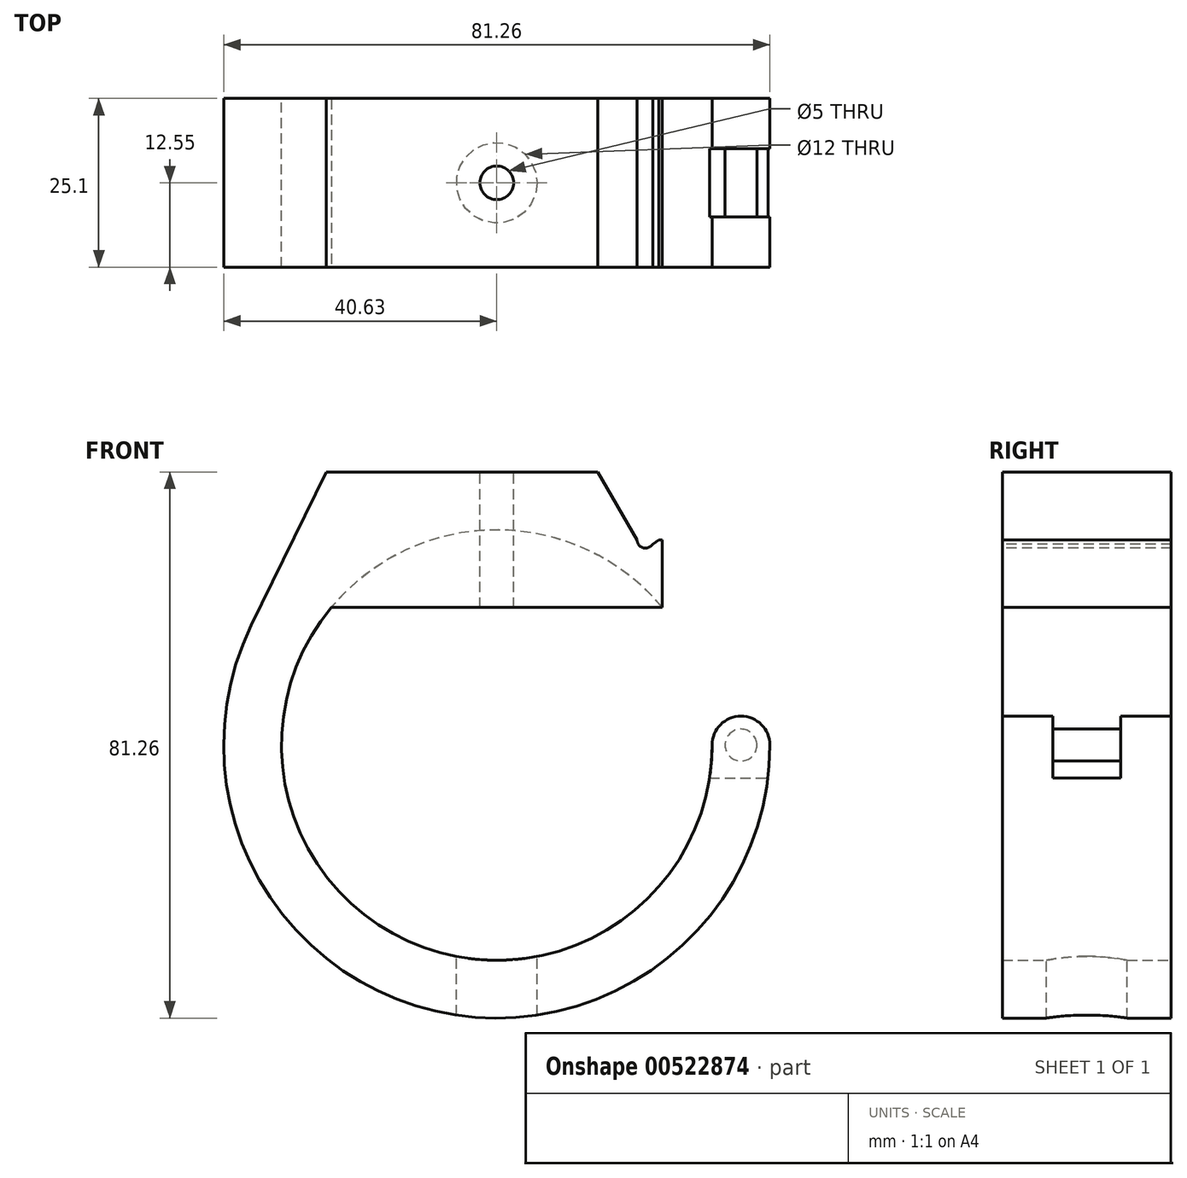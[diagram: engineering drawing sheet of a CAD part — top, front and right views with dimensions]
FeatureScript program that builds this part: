
annotation { "Feature Type Name" : "Feature", "Feature Type Description" : "" }
export const myFeature = defineFeature(function(context is Context, id is Id, definition is map)
    precondition{}
    {
        {
            var Q0;
            Q0=qCreatedBy(makeId("Front.planeOp"),FACE);
            var sketch = newSketch(context, id + "F0", { "sketchPlane" : qUnion([Q0])});
            skLineSegment(sketch, "E0.bottom", {"start": v(-25.4, 40.62) * mm, "end": v(24.6, 40.62) * mm});
            skLineSegment(sketch, "E0.left", {"start": v(-25.4, 40.62) * mm, "end": v(-25.4, 31.71) * mm});
            skLineSegment(sketch, "E0.right", {"start": v(24.6, 40.62) * mm, "end": v(24.6, 32.32) * mm});
            skPoint(sketch, "E0.middle", {"position": v(0, 0) * mm});
            skArc(sketch, "E1", {"start": v(-25.4, 31.71) * mm, "mid": v(0.5, -40.62) * mm, "end": v(24.6, 32.32) * mm});
            skCircle(sketch, "E2", {"center": v(0, 0) * mm, "radius": 32.02 * mm});
            skLineSegment(sketch, "E3", {"start": v(32.02, 0) * mm, "end": v(40.62, 0) * mm});
            skCircle(sketch, "E4", {"center": v(36.32, 0) * mm, "radius": 2.38 * mm});
            skCircle(sketch, "E5", {"center": v(36.32, 0) * mm, "radius": 4.3 * mm});
            skLineSegment(sketch, "E6", {"start": v(24.6, 32.32) * mm, "end": v(24.6, 20.49) * mm});
            skLineSegment(sketch, "E7", {"start": v(40.33, -4.92) * mm, "end": v(31.64, -4.92) * mm});
            skLineSegment(sketch, "E8", {"start": v(-25.4, 40.62) * mm, "end": v(-36.52, 17.8) * mm});
            skSolve(sketch);
        }
        {
            var Q0;
            Q0=makeQuery(id+"F0.imprint","IMPRINT",FACE,{"disambiguationData":[TD([[makeQuery(id+"F0.imprint","IMPRINT",EDGE,{"derivedFrom":sQuery(id+"F0.wireOp",EDGE,"E0.bottom")}),-1.0]])]});
            var Q1;
            {var subQ4=sQuery(id+"F0.wireOp",EDGE,"E7");Q1=makeQuery(id+"F0.imprint","IMPRINT",FACE,{"disambiguationData":[TD([[makeQuery(id+"F0.imprint","IMPRINT",EDGE,{"derivedFrom":subQ4}),-1.0]])]});}
            var Q2;
            {var subQ1=sQuery(id+"F0.wireOp",EDGE,"E3");var subQ3=sQuery(id+"F0.wireOp",EDGE,"E4");var subQ4=makeQuery(id+"F0.imprint","INTERSECT",VERTEX,{"disambiguationData":[OD(0.0)],"derivedFrom":[subQ1,subQ3]});Q2=makeQuery(id+"F0.imprint","IMPRINT",FACE,{"disambiguationData":[TD([[makeQuery(id+"F0.imprint","IMPRINT",EDGE,{"disambiguationData":[TD([[subQ4,1.0]])],"derivedFrom":subQ3}),-1.0]])]});}
            var Q3;
            {var subQ1=sQuery(id+"F0.wireOp",EDGE,"E3");var subQ3=sQuery(id+"F0.wireOp",EDGE,"E4");var subQ4=makeQuery(id+"F0.imprint","INTERSECT",VERTEX,{"disambiguationData":[OD(0.0)],"derivedFrom":[subQ1,subQ3]});Q3=makeQuery(id+"F0.imprint","IMPRINT",FACE,{"disambiguationData":[TD([[makeQuery(id+"F0.imprint","IMPRINT",EDGE,{"disambiguationData":[TD([[subQ4,-1.0]])],"derivedFrom":subQ3}),-1.0]])]});}
            extrude(context, id + "F1", {"entities" : qUnion([Q0, Q1, Q2, Q3]), "depth" : 7.5 * mm, "offsetDistance" : 25 * mm});
        }
        {
            var Q0;
            Q0=makeQuery(id+"F0.imprint","IMPRINT",FACE,{"disambiguationData":[TD([[makeQuery(id+"F0.imprint","IMPRINT",EDGE,{"derivedFrom":sQuery(id+"F0.wireOp",EDGE,"E0.bottom")}),-1.0]])]});
            extrude(context, id + "F2", {"entities" : qUnion([Q0]), "operationType" : NewBodyOperationType.ADD, "depth" : 17.6 * mm, "offsetDistance" : 25 * mm});
        }
        {
            var Q0;
            Q0=makeQuery(id+"F2.opExtrude","CAP_FACE",FACE,{"disambiguationData":[OSD([sQuery(id+"F0.wireOp",EDGE,"E0.bottom"),sQuery(id+"F0.wireOp",EDGE,"E0.left"),sQuery(id+"F0.wireOp",EDGE,"E0.right"),sQuery(id+"F0.wireOp",EDGE,"E1"),sQuery(id+"F0.wireOp",EDGE,"E2"),sQuery(id+"F0.wireOp",EDGE,"E6"),sQuery(id+"F0.wireOp",EDGE,"E7")])],"isStart":false});
            var sketch = newSketch(context, id + "F3", { "sketchPlane" : qUnion([Q0])});
            skLineSegment(sketch, "E9.bottom", {"start": v(-25.4, 40.63) * mm, "end": v(24.6, 40.63) * mm});
            skLineSegment(sketch, "E9.left", {"start": v(-25.4, 40.63) * mm, "end": v(-25.4, 31.71) * mm});
            skLineSegment(sketch, "E9.right", {"start": v(24.6, 40.63) * mm, "end": v(24.6, 32.32) * mm});
            skPoint(sketch, "E9.middle", {"position": v(0, 0) * mm});
            skArc(sketch, "E10", {"start": v(-25.4, 31.71) * mm, "mid": v(0.5, -40.62) * mm, "end": v(24.6, 32.32) * mm});
            skCircle(sketch, "E11", {"center": v(0, 0) * mm, "radius": 32.02 * mm});
            skLineSegment(sketch, "E12", {"start": v(32.02, 0) * mm, "end": v(40.63, 0) * mm});
            skCircle(sketch, "E13", {"center": v(36.32, 0) * mm, "radius": 2.38 * mm});
            skCircle(sketch, "E14", {"center": v(36.32, 0) * mm, "radius": 4.3 * mm});
            skLineSegment(sketch, "E15", {"start": v(24.6, 32.32) * mm, "end": v(24.6, 20.49) * mm});
            skLineSegment(sketch, "E16", {"start": v(40.33, -4.92) * mm, "end": v(31.64, -4.92) * mm});
            skSolve(sketch);
        }
        {
            var Q0;
            Q0=makeQuery(id+"F3.imprint","IMPRINT",FACE,{"disambiguationData":[TD([[makeQuery(id+"F3.imprint","IMPRINT",EDGE,{"derivedFrom":sQuery(id+"F3.wireOp",EDGE,"E9.bottom")}),-1.0]])]});
            var Q1;
            {var subQ0=sQuery(id+"F3.wireOp",EDGE,"E16");Q1=makeQuery(id+"F3.imprint","IMPRINT",FACE,{"disambiguationData":[TD([[makeQuery(id+"F3.imprint","IMPRINT",EDGE,{"derivedFrom":subQ0}),-1.0]])]});}
            var Q2;
            {var subQ1=sQuery(id+"F3.wireOp",EDGE,"E12");var subQ3=sQuery(id+"F3.wireOp",EDGE,"E13");var subQ4=makeQuery(id+"F3.imprint","INTERSECT",VERTEX,{"disambiguationData":[OD(0.0)],"derivedFrom":[subQ1,subQ3]});Q2=makeQuery(id+"F3.imprint","IMPRINT",FACE,{"disambiguationData":[TD([[makeQuery(id+"F3.imprint","IMPRINT",EDGE,{"disambiguationData":[TD([[subQ4,-1.0]])],"derivedFrom":subQ3}),-1.0]])]});}
            var Q3;
            {var subQ1=sQuery(id+"F3.wireOp",EDGE,"E12");var subQ3=sQuery(id+"F3.wireOp",EDGE,"E13");var subQ4=makeQuery(id+"F3.imprint","INTERSECT",VERTEX,{"disambiguationData":[OD(0.0)],"derivedFrom":[subQ1,subQ3]});Q3=makeQuery(id+"F3.imprint","IMPRINT",FACE,{"disambiguationData":[TD([[makeQuery(id+"F3.imprint","IMPRINT",EDGE,{"disambiguationData":[TD([[subQ4,1.0]])],"derivedFrom":subQ3}),-1.0]])]});}
            extrude(context, id + "F4", {"entities" : qUnion([Q0, Q1, Q2, Q3]), "operationType" : NewBodyOperationType.ADD, "depth" : 7.5 * mm, "offsetDistance" : 25 * mm});
        }
        {
            var Q0;
            Q0=makeQuery(id+"F4.opExtrude","CAP_FACE",FACE,{"disambiguationData":[OSD([sQuery(id+"F3.wireOp",EDGE,"E9.bottom"),sQuery(id+"F3.wireOp",EDGE,"E9.left"),sQuery(id+"F3.wireOp",EDGE,"E9.right"),sQuery(id+"F3.wireOp",EDGE,"E10"),sQuery(id+"F3.wireOp",EDGE,"E11"),sQuery(id+"F3.wireOp",EDGE,"E13"),sQuery(id+"F3.wireOp",EDGE,"E14"),sQuery(id+"F3.wireOp",EDGE,"E15")])],"isStart":false});
            var sketch = newSketch(context, id + "F5", { "sketchPlane" : qUnion([Q0])});
            skLineSegment(sketch, "E17", {"start": v(24.6, 20.49) * mm, "end": v(-24.6, 20.49) * mm});
            skSolve(sketch);
        }
        {
            var Q0;
            {var subQ0=sQuery(id+"F5.wireOp",EDGE,"E17");Q0=makeQuery(id+"F5.imprint","IMPRINT",FACE,{"disambiguationData":[TD([[makeQuery(id+"F5.imprint","IMPRINT",EDGE,{"derivedFrom":subQ0}),-1.0]])]});}
            extrude(context, id + "F6", {"entities" : qUnion([Q0]), "operationType" : NewBodyOperationType.ADD, "oppositeDirection" : true, "depth" : 25 * mm, "offsetDistance" : 25 * mm});
        }
        {
            var Q0;
            {var subQ0=sQuery(id+"F0.wireOp",EDGE,"E4");var subQ1=sQuery(id+"F0.wireOp",EDGE,"E3");var subQ2=makeQuery(id+"F0.imprint","INTERSECT",VERTEX,{"disambiguationData":[OD(0.0)],"derivedFrom":[subQ1,subQ0]});Q0=makeQuery(id+"F0.imprint","IMPRINT",FACE,{"disambiguationData":[TD([[makeQuery(id+"F0.imprint","IMPRINT",EDGE,{"disambiguationData":[TD([[subQ2,-1.0]])],"derivedFrom":subQ1}),1.0]])]});}
            var Q1;
            {var subQ0=sQuery(id+"F0.wireOp",EDGE,"E4");var subQ1=sQuery(id+"F0.wireOp",EDGE,"E3");var subQ2=makeQuery(id+"F0.imprint","INTERSECT",VERTEX,{"disambiguationData":[OD(0.0)],"derivedFrom":[subQ1,subQ0]});Q1=makeQuery(id+"F0.imprint","IMPRINT",FACE,{"disambiguationData":[TD([[makeQuery(id+"F0.imprint","IMPRINT",EDGE,{"disambiguationData":[TD([[subQ2,-1.0]])],"derivedFrom":subQ1}),-1.0]])]});}
            extrude(context, id + "F7", {"entities" : qUnion([Q0, Q1]), "operationType" : NewBodyOperationType.ADD, "depth" : 25.1 * mm, "offsetDistance" : 25 * mm});
        }
        {
            var Q0;
            {var subQ0=sQuery(id+"F0.wireOp",EDGE,"E0.bottom");Q0=makeQuery(id+"F4.boolean.opBoolean","MERGE",FACE,{"derivedFrom":[makeQuery(id+"F2.boolean.opBoolean","MERGE",FACE,{"derivedFrom":[makeQuery(id+"F1.opExtrude","SWEPT_FACE",FACE,{"disambiguationData":[OSD([subQ0])]}),makeQuery(id+"F2.opExtrude","SWEPT_FACE",FACE,{"disambiguationData":[OSD([subQ0])]})]}),makeQuery(id+"F4.opExtrude","SWEPT_FACE",FACE,{"disambiguationData":[OSD([sQuery(id+"F3.wireOp",EDGE,"E9.bottom")])]})]});}
            var sketch = newSketch(context, id + "F8", { "sketchPlane" : qUnion([Q0])});
            skCircle(sketch, "E18", {"center": v(0, -12.55) * mm, "radius": 2.5 * mm});
            skPoint(sketch, "E18.centerSnap0", {"position": v(-25.4, -12.55) * mm});
            skSolve(sketch);
        }
        {
            var Q0;
            Q0=makeQuery(id+"F8.imprint","IMPRINT",FACE,{"disambiguationData":[TD([[makeQuery(id+"F8.imprint","IMPRINT",EDGE,{"derivedFrom":sQuery(id+"F8.wireOp",EDGE,"E18")}),1.0]])]});
            extrude(context, id + "F9", {"entities" : qUnion([Q0]), "operationType" : NewBodyOperationType.REMOVE, "oppositeDirection" : true, "depth" : 121.4 * mm, "offsetDistance" : 25 * mm});
        }
        {
            var Q0;
            {var subQ0=sQuery(id+"F0.wireOp",EDGE,"E0.left");Q0=makeQuery(id+"F0.imprint","IMPRINT",FACE,{"disambiguationData":[TD([[makeQuery(id+"F0.imprint","IMPRINT",EDGE,{"derivedFrom":subQ0}),-1.0]])]});}
            extrude(context, id + "F10", {"entities" : qUnion([Q0]), "operationType" : NewBodyOperationType.ADD, "depth" : 25.1 * mm, "offsetDistance" : 25 * mm});
        }
        {
            var Q0;
            Q0=makeQuery(id+"F6.opExtrude","SWEPT_FACE",FACE,{"disambiguationData":[OSD([sQuery(id+"F5.wireOp",EDGE,"E17")])]});
            var sketch = newSketch(context, id + "F11", { "sketchPlane" : qUnion([Q0])});
            skCircle(sketch, "E19", {"center": v(0, 12.55) * mm, "radius": 6 * mm});
            skSolve(sketch);
        }
        {
            var Q0;
            Q0=makeQuery(id+"F11.imprint","IMPRINT",FACE,{"disambiguationData":[TD([[makeQuery(id+"F11.imprint","IMPRINT",EDGE,{"derivedFrom":sQuery(id+"F11.wireOp",EDGE,"E19")}),1.0]])]});
            extrude(context, id + "F12", {"entities" : qUnion([Q0]), "operationType" : NewBodyOperationType.REMOVE, "depth" : 82 * mm, "offsetDistance" : 25 * mm});
        }
        {
            var Q0;
            {var subQ0=sQuery(id+"F3.wireOp",EDGE,"E11");Q0=makeQuery(id+"F10.boolean.opBoolean","MERGE",FACE,{"derivedFrom":[makeQuery(id+"F7.boolean.opBoolean","MERGE",FACE,{"derivedFrom":[makeQuery(id+"F6.boolean.opBoolean","MERGE",FACE,{"derivedFrom":[makeQuery(id+"F4.opExtrude","CAP_FACE",FACE,{"disambiguationData":[OSD([sQuery(id+"F3.wireOp",EDGE,"E9.bottom"),sQuery(id+"F3.wireOp",EDGE,"E9.left"),sQuery(id+"F3.wireOp",EDGE,"E9.right"),sQuery(id+"F3.wireOp",EDGE,"E10"),subQ0,sQuery(id+"F3.wireOp",EDGE,"E13"),sQuery(id+"F3.wireOp",EDGE,"E14"),sQuery(id+"F3.wireOp",EDGE,"E15")])],"isStart":false}),makeQuery(id+"F6.opExtrude","CAP_FACE",FACE,{"disambiguationData":[OSD([subQ0,sQuery(id+"F5.wireOp",EDGE,"E17")])],"isStart":true})]}),makeQuery(id+"F7.opExtrude","CAP_FACE",FACE,{"disambiguationData":[OSD([sQuery(id+"F0.wireOp",EDGE,"E4")])],"isStart":false})]}),makeQuery(id+"F10.opExtrude","CAP_FACE",FACE,{"disambiguationData":[OSD([sQuery(id+"F0.wireOp",EDGE,"E0.left"),sQuery(id+"F0.wireOp",EDGE,"E1"),sQuery(id+"F0.wireOp",EDGE,"E8")])],"isStart":false})]});}
            var sketch = newSketch(context, id + "F13", { "sketchPlane" : qUnion([Q0])});
            skCircle(sketch, "E20", {"center": v(22.1, 30.56) * mm, "radius": 1.25 * mm});
            skLineSegment(sketch, "E21", {"start": v(22.1, 30.56) * mm, "end": v(24.6, 30.56) * mm});
            skLineSegment(sketch, "E22", {"start": v(20.86, 30.56) * mm, "end": v(15.02, 40.62) * mm});
            skLineSegment(sketch, "E23", {"start": v(24.09, 30.56) * mm, "end": v(23.18, 29.92) * mm});
            skSolve(sketch);
        }
        {
            var Q0;
            {var subQ0=sQuery(id+"F13.wireOp",EDGE,"Qatjs5W3-ByyJ-ekno-y4yl-Glvkwh5NXvYI");Q0=makeQuery(id+"F13.imprint","IMPRINT",FACE,{"disambiguationData":[TD([[makeQuery(id+"F13.imprint","IMPRINT",EDGE,{"derivedFrom":subQ0}),-1.0]])]});}
            var Q1;
            {var subQ0=sQuery(id+"F13.wireOp",EDGE,"Qatjs5W3-ByyJ-ekno-y4yl-Glvkwh5NXvYI");var subQ1=makeQuery(id+"F4.opExtrude","CAP_EDGE",EDGE,{"disambiguationData":[OSD([sQuery(id+"F3.wireOp",EDGE,"E9.bottom")])],"isStart":false});var subQ2=makeQuery(id+"F13.imprint","INTERSECT",VERTEX,{"derivedFrom":[subQ1,subQ0]});Q1=makeQuery(id+"F13.imprint","IMPRINT",FACE,{"disambiguationData":[TD([[makeQuery(id+"F13.imprint","IMPRINT",EDGE,{"disambiguationData":[TD([[subQ2,1.0]])],"derivedFrom":subQ0}),-1.0]])]});}
            var Q2;
            {var subQ0=sQuery(id+"F13.wireOp",EDGE,"E20");var subQ1=sQuery(id+"F13.wireOp",EDGE,"Qatjs5W3-ByyJ-ekno-y4yl-Glvkwh5NXvYI");var subQ3=makeQuery(id+"F13.imprint","INTERSECT",VERTEX,{"derivedFrom":[subQ1,subQ0]});Q2=makeQuery(id+"F13.imprint","IMPRINT",FACE,{"disambiguationData":[TD([[makeQuery(id+"F13.imprint","IMPRINT",EDGE,{"disambiguationData":[TD([[subQ3,1.0]])],"derivedFrom":subQ1}),1.0]])]});}
            var Q3;
            {var subQ3=sQuery(id+"F13.wireOp",EDGE,"wZKPCD1r-Sr3S-9iMm-FMkd-cQWfdQn9WrTu");var subQ5=sQuery(id+"F13.wireOp",EDGE,"E20");var subQ6=makeQuery(id+"F13.imprint","INTERSECT",VERTEX,{"derivedFrom":[subQ5,subQ3]});Q3=makeQuery(id+"F13.imprint","IMPRINT",FACE,{"disambiguationData":[TD([[makeQuery(id+"F13.imprint","IMPRINT",EDGE,{"disambiguationData":[TD([[subQ6,1.0]])],"derivedFrom":subQ5}),-1.0]])]});}
            var Q4;
            {var subQ0=sQuery(id+"F13.wireOp",EDGE,"wZKPCD1r-Sr3S-9iMm-FMkd-cQWfdQn9WrTu");var subQ1=sQuery(id+"F13.wireOp",EDGE,"E20");var subQ2=makeQuery(id+"F13.imprint","INTERSECT",VERTEX,{"derivedFrom":[subQ1,subQ0]});Q4=makeQuery(id+"F13.imprint","IMPRINT",FACE,{"disambiguationData":[TD([[makeQuery(id+"F13.imprint","IMPRINT",EDGE,{"disambiguationData":[TD([[subQ2,1.0]])],"derivedFrom":subQ1}),1.0]])]});}
            var Q5;
            {var subQ0=sQuery(id+"F13.wireOp",EDGE,"wZKPCD1r-Sr3S-9iMm-FMkd-cQWfdQn9WrTu");var subQ1=sQuery(id+"F13.wireOp",EDGE,"E20");var subQ2=makeQuery(id+"F13.imprint","INTERSECT",VERTEX,{"derivedFrom":[subQ1,subQ0]});Q5=makeQuery(id+"F13.imprint","IMPRINT",FACE,{"disambiguationData":[TD([[makeQuery(id+"F13.imprint","IMPRINT",EDGE,{"disambiguationData":[TD([[subQ2,-1.0]])],"derivedFrom":subQ1}),1.0]])]});}
            var Q6;
            {var subQ8=sQuery(id+"F13.wireOp",EDGE,"E22");Q6=makeQuery(id+"F13.imprint","IMPRINT",FACE,{"disambiguationData":[TD([[makeQuery(id+"F13.imprint","IMPRINT",EDGE,{"derivedFrom":subQ8}),-1.0]])]});}
            extrude(context, id + "F14", {"entities" : qUnion([Q0, Q1, Q2, Q3, Q4, Q5, Q6]), "operationType" : NewBodyOperationType.REMOVE, "oppositeDirection" : true, "depth" : 25.1 * mm, "offsetDistance" : 25 * mm});
        }
    });
